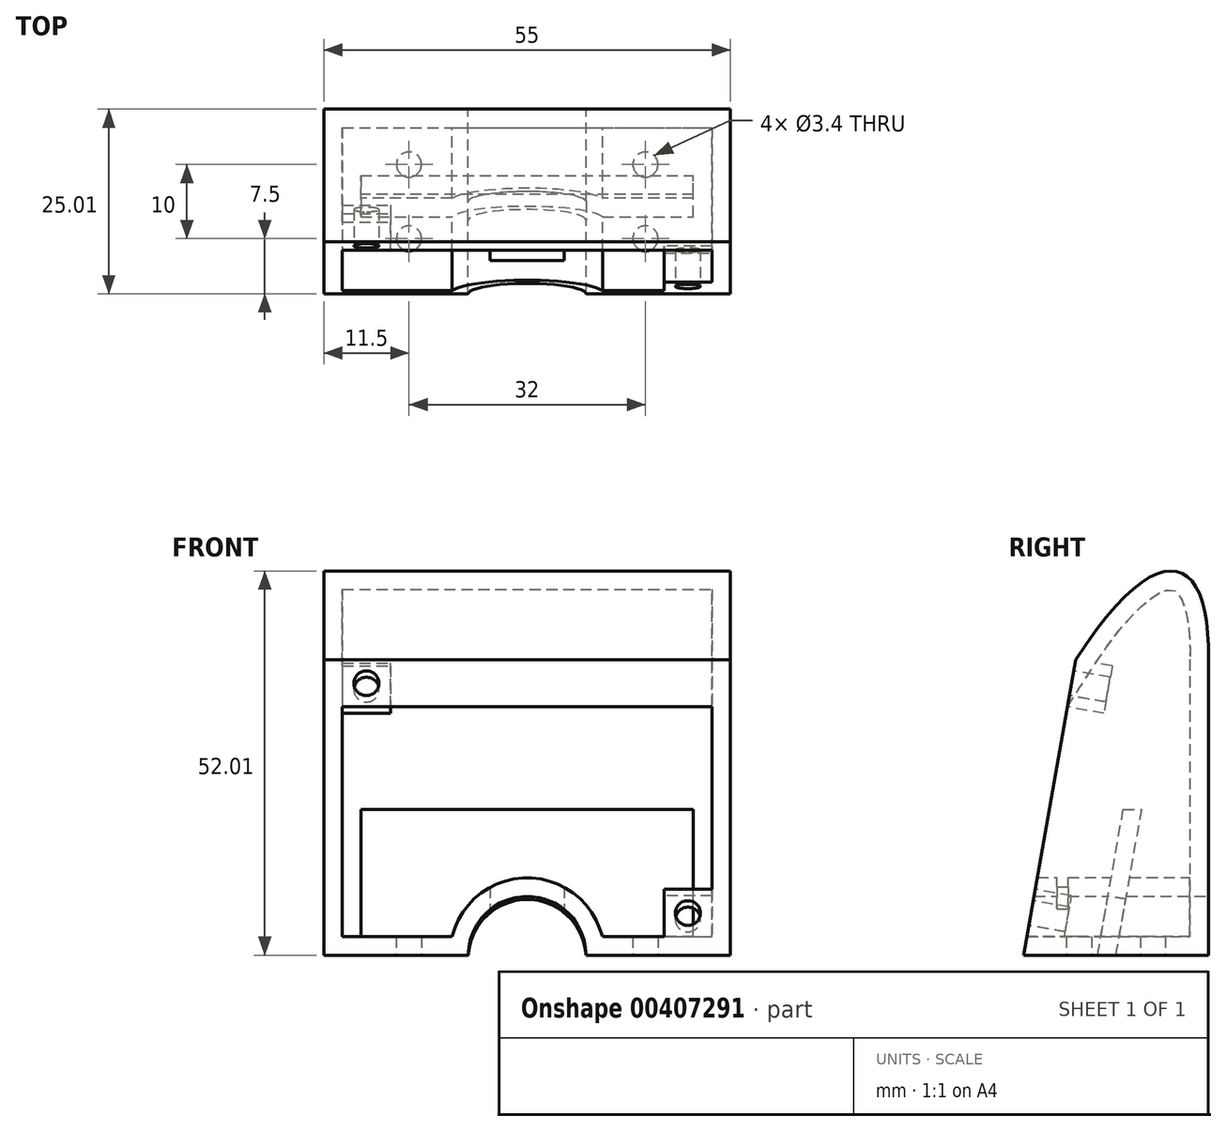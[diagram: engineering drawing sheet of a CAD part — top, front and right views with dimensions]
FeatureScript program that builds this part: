
annotation { "Feature Type Name" : "Feature", "Feature Type Description" : "" }
export const myFeature = defineFeature(function(context is Context, id is Id, definition is map)
    precondition{}
    {
        {
            var Q0;
            Q0=qCreatedBy(makeId("Top.planeOp"),FACE);
            var sketch = newSketch(context, id + "F0", { "sketchPlane" : qUnion([Q0])});
            skLineSegment(sketch, "E0.bottom", {"start": v(0, 0) * mm, "end": v(55, 0) * mm});
            skLineSegment(sketch, "E0.top", {"start": v(0, -25) * mm, "end": v(55, -25) * mm});
            skLineSegment(sketch, "E0.left", {"start": v(0, 0) * mm, "end": v(0, -25) * mm});
            skLineSegment(sketch, "E0.right", {"start": v(55, 0) * mm, "end": v(55, -25) * mm});
            skLineSegment(sketch, "E1", {"start": v(27.5, 0) * mm, "end": v(27.5, -15) * mm});
            skLineSegment(sketch, "E2", {"start": v(27.5, -15) * mm, "end": v(50, -15) * mm});
            skLineSegment(sketch, "E3.MirrorCS", {"start": v(27.5, -15) * mm, "end": v(5, -15) * mm});
            skLineSegment(sketch, "E4", {"start": v(5, -12.5) * mm, "end": v(5, -15) * mm});
            skPoint(sketch, "E4.endSnap0", {"position": v(0, -12.5) * mm});
            skLineSegment(sketch, "E5", {"start": v(5, -12.5) * mm, "end": v(50, -12.5) * mm});
            skLineSegment(sketch, "E6", {"start": v(50, -15) * mm, "end": v(50, -12.5) * mm});
            skLineSegment(sketch, "E7", {"start": v(27.5, -15) * mm, "end": v(27.5, -19) * mm});
            skLineSegment(sketch, "E8", {"start": v(27.5, -19) * mm, "end": v(32.5, -19) * mm});
            skLineSegment(sketch, "E9", {"start": v(32.5, -19) * mm, "end": v(32.5, -20.5) * mm});
            skLineSegment(sketch, "E10", {"start": v(32.5, -20.5) * mm, "end": v(27.5, -20.5) * mm});
            skLineSegment(sketch, "E11.MirrorCS", {"start": v(27.5, -19) * mm, "end": v(22.5, -19) * mm});
            skLineSegment(sketch, "E12.MirrorCS", {"start": v(22.5, -19) * mm, "end": v(22.5, -20.5) * mm});
            skLineSegment(sketch, "E13.MirrorCS", {"start": v(22.5, -20.5) * mm, "end": v(27.5, -20.5) * mm});
            skSolve(sketch);
        }
        {
            var Q0;
            Q0 = qSketchRegion(id + "F0", true);
            extrude(context, id + "F1", {"entities" : qUnion([Q0]), "depth" : 40 * mm});
        }
        {
            var Q0;
            Q0=makeQuery(id+"F1.opExtrude","SWEPT_FACE",FACE,{"disambiguationData":[OSD([sQuery(id+"F0.wireOp",EDGE,"E0.right")])]});
            var sketch = newSketch(context, id + "F2", { "sketchPlane" : qUnion([Q0])});
            skLineSegment(sketch, "E14", {"start": v(-25, 0) * mm, "end": v(-17.95, 40) * mm});
            skSolve(sketch);
        }
        {
            var Q0;
            {var subQ0=sQuery(id+"F2.wireOp",EDGE,"E14");Q0=makeQuery(id+"F2.imprint","IMPRINT",FACE,{"disambiguationData":[TD([[makeQuery(id+"F2.imprint","IMPRINT",EDGE,{"derivedFrom":subQ0}),1.0]])]});}
            extrude(context, id + "F3", {"entities" : qUnion([Q0]), "operationType" : NewBodyOperationType.REMOVE, "oppositeDirection" : true, "depth" : 55 * mm});
        }
        {
            var Q0;
            Q0=qCreatedBy(makeId("Top.planeOp"),FACE);
            var sketch = newSketch(context, id + "F4", { "sketchPlane" : qUnion([Q0])});
            skLineSegment(sketch, "E15", {"start": v(6.5, -12.6) * mm, "end": v(11.5, -12.6) * mm});
            skLineSegment(sketch, "E16", {"start": v(11.5, -12.6) * mm, "end": v(11.5, -7.6) * mm});
            skLineSegment(sketch, "E17", {"start": v(11.5, -7.6) * mm, "end": v(11.5, -17.6) * mm});
            skCircle(sketch, "E18", {"center": v(11.5, -7.6) * mm, "radius": 1.7 * mm});
            skCircle(sketch, "E19", {"center": v(11.5, -17.6) * mm, "radius": 1.7 * mm});
            skLineSegment(sketch, "E20", {"start": v(0, -2.6) * mm, "end": v(27.5, -2.6) * mm});
            skLineSegment(sketch, "E21", {"start": v(27.5, -2.6) * mm, "end": v(27.5, -12.6) * mm});
            skLineSegment(sketch, "E22.MirrorCS", {"start": v(43.5, -12.6) * mm, "end": v(43.5, -7.6) * mm});
            skLineSegment(sketch, "E23.MirrorCS", {"start": v(48.5, -12.6) * mm, "end": v(43.5, -12.6) * mm});
            skLineSegment(sketch, "E24.MirrorCS", {"start": v(43.5, -7.6) * mm, "end": v(43.5, -17.6) * mm});
            skCircle(sketch, "E25.MirrorC", {"center": v(43.5, -7.6) * mm, "radius": 1.7 * mm});
            skCircle(sketch, "E26.MirrorC", {"center": v(43.5, -17.6) * mm, "radius": 1.7 * mm});
            skCircle(sketch, "E27", {"center": v(27.5, -12.6) * mm, "radius": 1.7 * mm});
            skSolve(sketch);
        }
        {
            var Q0;
            Q0=makeQuery(id+"F4.imprint","IMPRINT",FACE,{"disambiguationData":[TD([[makeQuery(id+"F4.imprint","IMPRINT",EDGE,{"derivedFrom":sQuery(id+"F4.wireOp",EDGE,"E18")}),1.0]])]});
            var Q1;
            Q1=makeQuery(id+"F4.imprint","IMPRINT",FACE,{"disambiguationData":[TD([[makeQuery(id+"F4.imprint","IMPRINT",EDGE,{"derivedFrom":sQuery(id+"F4.wireOp",EDGE,"E19")}),1.0]])]});
            var Q2;
            Q2=makeQuery(id+"F4.imprint","IMPRINT",FACE,{"disambiguationData":[TD([[makeQuery(id+"F4.imprint","IMPRINT",EDGE,{"derivedFrom":sQuery(id+"F4.wireOp",EDGE,"E25.MirrorC")}),-1.0]])]});
            var Q3;
            Q3=makeQuery(id+"F4.imprint","IMPRINT",FACE,{"disambiguationData":[TD([[makeQuery(id+"F4.imprint","IMPRINT",EDGE,{"derivedFrom":sQuery(id+"F4.wireOp",EDGE,"E26.MirrorC")}),-1.0]])]});
            extrude(context, id + "F5", {"entities" : qUnion([Q0, Q1, Q2, Q3]), "operationType" : NewBodyOperationType.REMOVE, "depth" : 3.5 * mm});
        }
        {
            var Q0;
            Q0=makeQuery(id+"F1.opExtrude","SWEPT_FACE",FACE,{"disambiguationData":[OSD([sQuery(id+"F0.wireOp",EDGE,"E0.right")])]});
            var sketch = newSketch(context, id + "F6", { "sketchPlane" : qUnion([Q0])});
            skLineSegment(sketch, "E28", {"start": v(0, 0) * mm, "end": v(0, 40) * mm});
            skLineSegment(sketch, "E29", {"start": v(0, 40) * mm, "end": v(-17.95, 40) * mm});
            skFitSpline(sketch, "E30", {"points": [v(-17.95, 40) * mm, v(0, 40) * mm, v(3.25, 31.43) * mm], "startDerivative": vector(56.76, 88.55) * mm, "endDerivative": vector(54.69, 135.51) * mm});
            skSolve(sketch);
        }
        {
            var Q0;
            Q0 = qSketchRegion(id + "F6", true);
            var Q1;
            {var subQ4=sQuery(id+"F6.wireOp",EDGE,"E29");Q1=makeQuery(id+"F6.imprint","IMPRINT",FACE,{"disambiguationData":[TD([[makeQuery(id+"F6.imprint","IMPRINT",EDGE,{"derivedFrom":subQ4}),1.0]])]});}
            extrude(context, id + "F7", {"entities" : qUnion([Q0, Q1]), "operationType" : NewBodyOperationType.ADD, "oppositeDirection" : true, "depth" : 55 * mm});
        }
        {
            var Q0;
            Q0=makeQuery(id+"F1.opExtrude","SWEPT_FACE",FACE,{"disambiguationData":[OSD([sQuery(id+"F0.wireOp",EDGE,"E0.bottom")])]});
            var sketch = newSketch(context, id + "F8", { "sketchPlane" : qUnion([Q0])});
            skCircle(sketch, "E31", {"center": v(-27.5, 0) * mm, "radius": 8 * mm});
            skSolve(sketch);
        }
        {
            var Q0;
            Q0 = qSketchRegion(id + "F8", true);
            extrude(context, id + "F9", {"entities" : qUnion([Q0]), "operationType" : NewBodyOperationType.REMOVE, "oppositeDirection" : true, "depth" : 25 * mm});
        }
        {
            var Q0;
            Q0=makeQuery(id+"F3.boolean.opBoolean","COPY",FACE,{"derivedFrom":makeQuery(id+"F3.opExtrude","SWEPT_FACE",FACE,{"disambiguationData":[OSD([sQuery(id+"F2.wireOp",EDGE,"E14")])]})});
            shell(context, id + "F10", {"entities" : qUnion([Q0]), "thickness" : 2.5 * mm});
        }
        {
            var Q0;
            Q0=qCreatedBy(makeId("Right.planeOp"),FACE);
            cPlane(context, id + "F11", {"entities" : qUnion([Q0]), "cplaneType" : CPlaneType.OFFSET, "offset" : 5 * mm, "width" : 150 * mm, "height" : 150 * mm});
        }
        {
            var Q0;
            Q0=qCreatedBy(id+"F11.planeOp",FACE);
            var sketch = newSketch(context, id + "F12", { "sketchPlane" : qUnion([Q0])});
            skLineSegment(sketch, "E32", {"start": v(0, 0) * mm, "end": v(-15, 0) * mm});
            skLineSegment(sketch, "E33", {"start": v(-15, 0) * mm, "end": v(-11.53, 19.7) * mm});
            skSolve(sketch);
        }
        {
            var Q0;
            {var subQ0=sQuery(id+"F0.wireOp",EDGE,"E3.MirrorCS");Q0=makeQuery(id+"F0.imprint","IMPRINT",FACE,{"disambiguationData":[TD([[makeQuery(id+"F0.imprint","IMPRINT",EDGE,{"derivedFrom":subQ0}),-1.0]])]});}
            var Q1;
            {var subQ0=sQuery(id+"F0.wireOp",EDGE,"E2");Q1=makeQuery(id+"F0.imprint","IMPRINT",FACE,{"disambiguationData":[TD([[makeQuery(id+"F0.imprint","IMPRINT",EDGE,{"derivedFrom":subQ0}),1.0]])]});}
            var Q2;
            Q2=sQuery(id+"F12.wireOp",EDGE,"E33");
            sweep(context, id + "F13", {"operationType" : NewBodyOperationType.ADD, "profiles" : qUnion([Q0, Q1]), "path" : qUnion([Q2])});
        }
        {
            var Q0;
            Q0=makeQuery(id+"F3.boolean.opBoolean","COPY",FACE,{"derivedFrom":makeQuery(id+"F3.opExtrude","SWEPT_FACE",FACE,{"disambiguationData":[OSD([sQuery(id+"F2.wireOp",EDGE,"E14")])]})});
            var sketch = newSketch(context, id + "F14", { "sketchPlane" : qUnion([Q0])});
            skLineSegment(sketch, "E34.bottom", {"start": v(2.5, 36.28) * mm, "end": v(9, 36.28) * mm});
            skLineSegment(sketch, "E34.top", {"start": v(2.5, 29.79) * mm, "end": v(9, 29.79) * mm});
            skLineSegment(sketch, "E34.left", {"start": v(2.5, 36.28) * mm, "end": v(2.5, 29.79) * mm});
            skLineSegment(sketch, "E34.right", {"start": v(9, 36.28) * mm, "end": v(9, 29.79) * mm});
            skCircle(sketch, "E35", {"center": v(5.75, 33.03) * mm, "radius": 1.7 * mm});
            skPoint(sketch, "E35.centerSnap0", {"position": v(6.5, 33.03) * mm});
            skPoint(sketch, "E35.centerSnap1", {"position": v(3.25, 36.28) * mm});
            skLineSegment(sketch, "E36.bottom", {"start": v(52.5, -1.8) * mm, "end": v(46, -1.8) * mm});
            skLineSegment(sketch, "E36.top", {"start": v(52.5, 4.7) * mm, "end": v(46, 4.7) * mm});
            skLineSegment(sketch, "E36.left", {"start": v(52.5, -1.8) * mm, "end": v(52.5, 4.7) * mm});
            skLineSegment(sketch, "E36.right", {"start": v(46, -1.8) * mm, "end": v(46, 4.7) * mm});
            skCircle(sketch, "E37", {"center": v(49.25, 1.45) * mm, "radius": 1.7 * mm});
            skPoint(sketch, "E37.centerSnap0", {"position": v(48.5, -1.1) * mm});
            skPoint(sketch, "E37.centerSnap1", {"position": v(51.75, 2.16) * mm});
            skLineSegment(sketch, "E38.left", {"start": v(0, -4.34) * mm, "end": v(0, 36.28) * mm});
            skSolve(sketch);
        }
        {
            var Q0;
            Q0 = qSketchRegion(id + "F14", true);
            extrude(context, id + "F15", {"entities" : qUnion([Q0]), "operationType" : NewBodyOperationType.ADD, "oppositeDirection" : true, "depth" : 5 * mm});
        }
        {
            var Q0;
            Q0=makeQuery(id+"F14.imprint","IMPRINT",FACE,{"disambiguationData":[TD([[makeQuery(id+"F14.imprint","IMPRINT",EDGE,{"derivedFrom":sQuery(id+"F14.wireOp",EDGE,"E35")}),1.0]])]});
            var Q1;
            {var subQ0=sQuery(id+"F14.wireOp",EDGE,"E37");var subQ1=sQuery(id+"F2.wireOp",EDGE,"E14");var subQ2=makeQuery(id+"F10.opShell","OFFSET_EDGE",EDGE,{"disambiguationData":[OSD([subQ1]),TDD([makeQuery(id+"F3.boolean.opBoolean","COPY",EDGE,{"derivedFrom":makeQuery(id+"F3.opExtrude","CAP_EDGE",EDGE,{"disambiguationData":[OSD([subQ1])],"isStart":true})})])]});var subQ3=makeQuery(id+"F14.imprint","INTERSECT",VERTEX,{"derivedFrom":[subQ2,subQ0]});Q1=makeQuery(id+"F14.imprint","IMPRINT",FACE,{"disambiguationData":[TD([[makeQuery(id+"F14.imprint","IMPRINT",EDGE,{"disambiguationData":[TD([[subQ3,-1.0]])],"derivedFrom":subQ0}),1.0]])]});}
            var Q2;
            {var subQ0=sQuery(id+"F14.wireOp",EDGE,"E37");var subQ1=sQuery(id+"F2.wireOp",EDGE,"E14");var subQ2=makeQuery(id+"F10.opShell","OFFSET_EDGE",EDGE,{"disambiguationData":[OSD([subQ1]),TDD([makeQuery(id+"F3.boolean.opBoolean","COPY",EDGE,{"derivedFrom":makeQuery(id+"F3.opExtrude","CAP_EDGE",EDGE,{"disambiguationData":[OSD([subQ1])],"isStart":true})})])]});var subQ3=makeQuery(id+"F14.imprint","INTERSECT",VERTEX,{"derivedFrom":[subQ2,subQ0]});Q2=makeQuery(id+"F14.imprint","IMPRINT",FACE,{"disambiguationData":[TD([[makeQuery(id+"F14.imprint","IMPRINT",EDGE,{"disambiguationData":[TD([[subQ3,1.0]])],"derivedFrom":subQ0}),1.0]])]});}
            extrude(context, id + "F16", {"entities" : qUnion([Q0, Q1, Q2]), "operationType" : NewBodyOperationType.REMOVE, "oppositeDirection" : true, "depth" : 5 * mm});
        }
        {
            var Q0;
            Q0=makeQuery(id+"F7.boolean.opBoolean","MERGE",FACE,{"derivedFrom":[makeQuery(id+"F1.opExtrude","SWEPT_FACE",FACE,{"disambiguationData":[OSD([sQuery(id+"F0.wireOp",EDGE,"E0.left")])]}),makeQuery(id+"F7.opExtrude","CAP_FACE",FACE,{"disambiguationData":[OSD([sQuery(id+"F0.wireOp",EDGE,"E0.right"),sQuery(id+"F2.wireOp",EDGE,"E14"),sQuery(id+"F6.wireOp",EDGE,"E28"),sQuery(id+"F6.wireOp",EDGE,"E30")])],"isStart":false})]});
            var sketch = newSketch(context, id + "F17", { "sketchPlane" : qUnion([Q0])});
            skLineSegment(sketch, "E39.bottom", {"start": v(0, 0) * mm, "end": v(25, 0) * mm});
            skLineSegment(sketch, "E39.top", {"start": v(0, -1.74) * mm, "end": v(25, -1.74) * mm});
            skLineSegment(sketch, "E39.left", {"start": v(0, 0) * mm, "end": v(0, -1.74) * mm});
            skLineSegment(sketch, "E39.right", {"start": v(25, 0) * mm, "end": v(25, -1.74) * mm});
            skSolve(sketch);
        }
        {
            var Q0;
            Q0 = qSketchRegion(id + "F17", true);
            extrude(context, id + "F18", {"entities" : qUnion([Q0]), "operationType" : NewBodyOperationType.REMOVE, "oppositeDirection" : true, "depth" : 55 * mm});
        }
        {
            var Q0;
            {var subQ3=sQuery(id+"F0.wireOp",EDGE,"E3.MirrorCS");var subQ4=sQuery(id+"F0.wireOp",EDGE,"E2");var subQ5=sQuery(id+"F0.wireOp",EDGE,"E0.right");Q0=makeQuery(id+"F13.boolean.opBoolean","SPLIT",FACE,{"disambiguationData":[TD([makeQuery(id+"F7.opExtrude","SWEPT_FACE",FACE,{"disambiguationData":[OSD([subQ5])]})])],"derivedFrom":makeQuery(id+"F13.opSweep","SWEPT_FACE",FACE,{"disambiguationData":[OSD([subQ4,subQ3,sQuery(id+"F12.wireOp",EDGE,"E33")])]})});}
            extrude(context, id + "F19", {"entities" : qUnion([Q0]), "operationType" : NewBodyOperationType.REMOVE, "oppositeDirection" : true, "depth" : 2.5 * mm});
        }
        {
            var Q0;
            {var subQ3=sQuery(id+"F0.wireOp",EDGE,"E0.right");var subQ8=sQuery(id+"F0.wireOp",EDGE,"E3.MirrorCS");var subQ9=sQuery(id+"F0.wireOp",EDGE,"E2");var subQ10=sQuery(id+"F0.wireOp",EDGE,"E0.left");var subQ11=makeQuery(id+"F1.opExtrude","SWEPT_FACE",FACE,{"disambiguationData":[OSD([subQ10])]});var subQ12=sQuery(id+"F0.wireOp",EDGE,"E0.bottom");var subQ15=sQuery(id+"F0.wireOp",EDGE,"E5");var subQ16=sQuery(id+"F0.wireOp",EDGE,"E6");var subQ17=sQuery(id+"F0.wireOp",EDGE,"E4");var subQ18=makeQuery(id+"F7.boolean.opBoolean","MERGE",FACE,{"derivedFrom":[makeQuery(id+"F1.opExtrude","CAP_FACE",FACE,{"disambiguationData":[OSD([subQ12,sQuery(id+"F0.wireOp",EDGE,"E0.top"),subQ10,subQ3,subQ9,subQ8,subQ17,subQ15,subQ16])],"isStart":true}),makeQuery(id+"F7.opExtrude","SWEPT_FACE",FACE,{"disambiguationData":[OSD([subQ3])]})]});Q0=makeQuery(id+"F19.boolean.opBoolean","SPLIT",FACE,{"disambiguationData":[TD([subQ11])],"derivedFrom":makeQuery(id+"F13.boolean.opBoolean","MERGE",FACE,{"derivedFrom":[makeQuery(id+"F9.boolean.opBoolean","SPLIT",FACE,{"disambiguationData":[TD([subQ11])],"derivedFrom":subQ18}),makeQuery(id+"F9.boolean.opBoolean","SPLIT",FACE,{"disambiguationData":[TD([makeQuery(id+"F1.opExtrude","SWEPT_FACE",FACE,{"disambiguationData":[OSD([subQ3])]})])],"derivedFrom":subQ18}),makeQuery(id+"F13.opSweep","CAP_FACE",FACE,{"disambiguationData":[OSD([subQ9,subQ8,subQ17,subQ15,subQ16,sQuery(id+"F12.wireOp",VERTEX,"E33.start")])],"isStart":true})]})});}
            var sketch = newSketch(context, id + "F20", { "sketchPlane" : qUnion([Q0])});
            skLineSegment(sketch, "E40", {"start": v(0, 12.5) * mm, "end": v(11.5, 12.5) * mm});
            skLineSegment(sketch, "E41", {"start": v(11.5, 12.5) * mm, "end": v(11.5, 17.5) * mm});
            skLineSegment(sketch, "E42", {"start": v(11.5, 12.5) * mm, "end": v(11.5, 7.5) * mm});
            skCircle(sketch, "E43", {"center": v(11.5, 17.5) * mm, "radius": 1.7 * mm});
            skCircle(sketch, "E44", {"center": v(11.5, 7.5) * mm, "radius": 1.7 * mm});
            skLineSegment(sketch, "E45.MirrorCS", {"start": v(43.5, 12.5) * mm, "end": v(43.5, 17.5) * mm});
            skLineSegment(sketch, "E46.MirrorCS", {"start": v(43.5, 12.5) * mm, "end": v(43.5, 7.5) * mm});
            skCircle(sketch, "E47.MirrorC", {"center": v(43.5, 17.5) * mm, "radius": 1.7 * mm});
            skCircle(sketch, "E48.MirrorC", {"center": v(43.5, 7.5) * mm, "radius": 1.7 * mm});
            skSolve(sketch);
        }
        {
            var Q0;
            Q0 = qSketchRegion(id + "F20", true);
            extrude(context, id + "F21", {"entities" : qUnion([Q0]), "operationType" : NewBodyOperationType.REMOVE, "oppositeDirection" : true, "depth" : 3.5 * mm});
        }
        {
            var Q0;
            Q0=makeQuery(id+"F0.imprint","IMPRINT",FACE,{"disambiguationData":[TD([[makeQuery(id+"F0.imprint","IMPRINT",EDGE,{"derivedFrom":sQuery(id+"F0.wireOp",EDGE,"E8")}),-1.0]])]});
            extrude(context, id + "F22", {"entities" : qUnion([Q0]), "operationType" : NewBodyOperationType.REMOVE, "depth" : 11 * mm});
        }
    });
